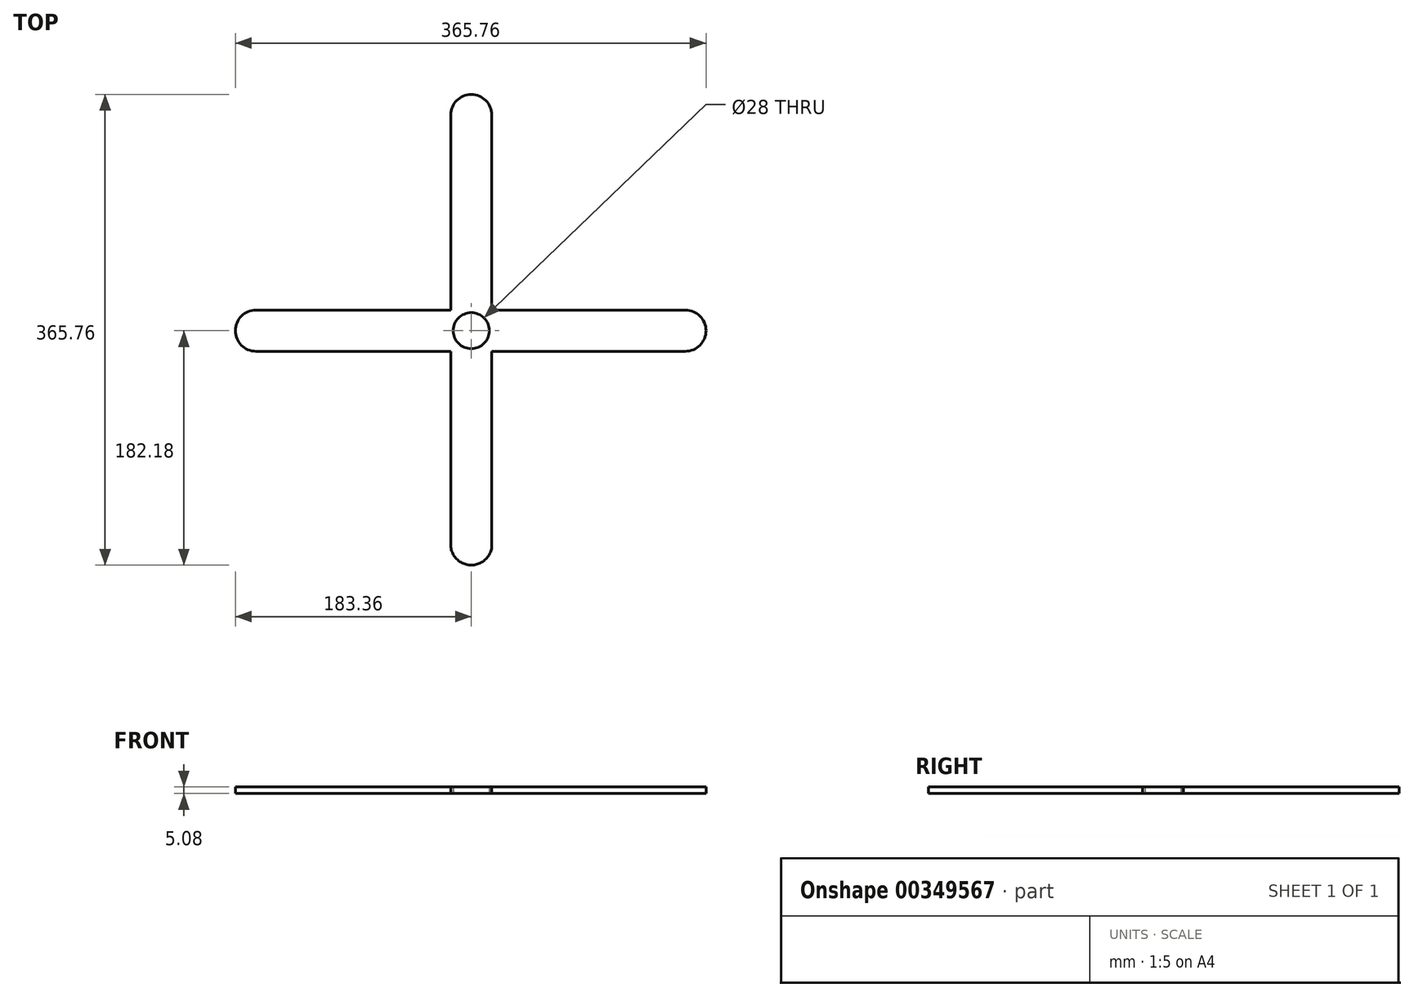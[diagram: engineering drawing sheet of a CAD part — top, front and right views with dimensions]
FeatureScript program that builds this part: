
annotation { "Feature Type Name" : "Feature", "Feature Type Description" : "" }
export const myFeature = defineFeature(function(context is Context, id is Id, definition is map)
    precondition{}
    {
        {
            var Q0;
            Q0=qCreatedBy(makeId("Top.planeOp"),FACE);
            var sketch = newSketch(context, id + "F0", { "sketchPlane" : qUnion([Q0])});
            skCircle(sketch, "E0", {"center": v(0, 0) * mm, "radius": 14 * mm});
            skLineSegment(sketch, "E1.left", {"start": v(-16, 167.58) * mm, "end": v(-16, -166.18) * mm});
            skLineSegment(sketch, "E1.right", {"start": v(16, 167.58) * mm, "end": v(16, -166.18) * mm});
            skPoint(sketch, "E1.middle", {"position": v(0, 0.7) * mm});
            skArc(sketch, "E2", {"start": v(16, -166.18) * mm, "mid": v(0, -182.18) * mm, "end": v(-16, -166.18) * mm});
            skArc(sketch, "E3", {"start": v(16, 167.58) * mm, "mid": v(0, 183.58) * mm, "end": v(-16, 167.58) * mm});
            skPoint(sketch, "E4", {"position": v(0, -182.18) * mm});
            skPoint(sketch, "E5", {"position": v(0, 183.58) * mm});
            skLineSegment(sketch, "E6", {"start": v(0, -182.18) * mm, "end": v(0, 183.58) * mm});
            skLineSegment(sketch, "E7", {"start": v(16, -166.18) * mm, "end": v(-16, -166.18) * mm});
            skLineSegment(sketch, "E8.left", {"start": v(-167.36, -16.02) * mm, "end": v(166.4, -16) * mm});
            skLineSegment(sketch, "E8.right", {"start": v(-167.36, 15.99) * mm, "end": v(166.4, 16) * mm});
            skPoint(sketch, "E8.middle", {"position": v(-0.48, 0) * mm});
            skArc(sketch, "E9", {"start": v(166.4, 16) * mm, "mid": v(182.4, 0) * mm, "end": v(166.4, -16) * mm});
            skArc(sketch, "E10", {"start": v(-167.36, 15.99) * mm, "mid": v(-183.36, -0.02) * mm, "end": v(-167.36, -16.02) * mm});
            skPoint(sketch, "E11", {"position": v(182.4, 0) * mm});
            skPoint(sketch, "E12", {"position": v(-183.36, -0.02) * mm});
            skLineSegment(sketch, "E13", {"start": v(182.4, 0) * mm, "end": v(-183.36, -0.02) * mm});
            skLineSegment(sketch, "E14", {"start": v(166.4, 16) * mm, "end": v(166.4, -16) * mm});
            skSolve(sketch);
        }
        {
            var Q0;
            Q0 = qSketchRegion(id + "F0", true);
            extrude(context, id + "F1", {"entities" : qUnion([Q0]), "depth" : 5.08 * mm});
        }
    });
